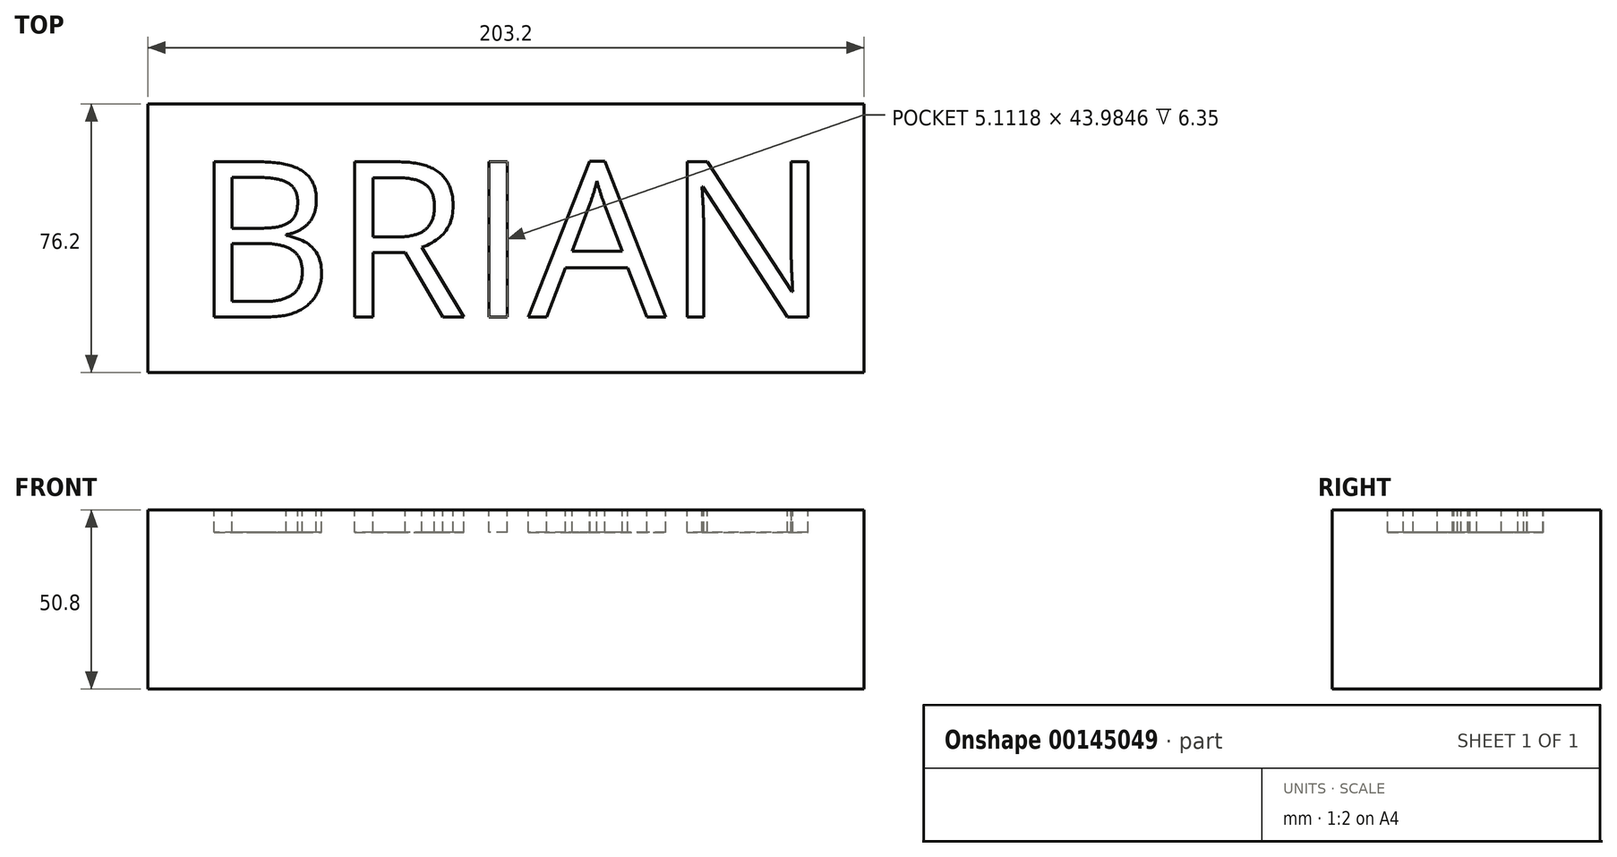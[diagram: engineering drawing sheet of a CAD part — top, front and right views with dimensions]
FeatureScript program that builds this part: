
annotation { "Feature Type Name" : "Feature", "Feature Type Description" : "" }
export const myFeature = defineFeature(function(context is Context, id is Id, definition is map)
    precondition{}
    {
        {
            var Q0;
            Q0=qCreatedBy(makeId("Top.planeOp"),FACE);
            var sketch = newSketch(context, id + "F0", { "sketchPlane" : qUnion([Q0])});
            skLineSegment(sketch, "E0.bottom", {"start": v(0, 76.2) * mm, "end": v(203.2, 76.2) * mm});
            skLineSegment(sketch, "E0.top", {"start": v(0, 0) * mm, "end": v(203.2, 0) * mm});
            skLineSegment(sketch, "E0.left", {"start": v(0, 76.2) * mm, "end": v(0, 0) * mm});
            skLineSegment(sketch, "E0.right", {"start": v(203.2, 76.2) * mm, "end": v(203.2, 0) * mm});
            skSolve(sketch);
        }
        {
            var Q0;
            Q0 = qSketchRegion(id + "F0", true);
            extrude(context, id + "F1", {"entities" : qUnion([Q0]), "depth" : 50.8 * mm});
        }
        {
            var Q0;
            Q0=makeQuery(id+"F1.opExtrude","CAP_FACE",FACE,{"disambiguationData":[OSD([sQuery(id+"F0.wireOp",EDGE,"E0.bottom"),sQuery(id+"F0.wireOp",EDGE,"E0.top"),sQuery(id+"F0.wireOp",EDGE,"E0.left"),sQuery(id+"F0.wireOp",EDGE,"E0.right")])],"isStart":false});
            var sketch = newSketch(context, id + "F2", { "sketchPlane" : qUnion([Q0])});
            skText(sketch, "E1", { "text": "BRIAN", "fontName": "OpenSans-Regular.ttf"});
            const initialGuessF2  = {"E1": [0.01278, 0.01579, 1, 0, 0.04436]};
            skSetInitialGuess(sketch, initialGuessF2);
            skSolve(sketch);
        }
        {
            var Q0;
            Q0 = qSketchRegion(id + "F2", true);
            extrude(context, id + "F3", {"entities" : qUnion([Q0]), "operationType" : NewBodyOperationType.REMOVE, "oppositeDirection" : true, "depth" : 6.35 * mm});
        }
    });
